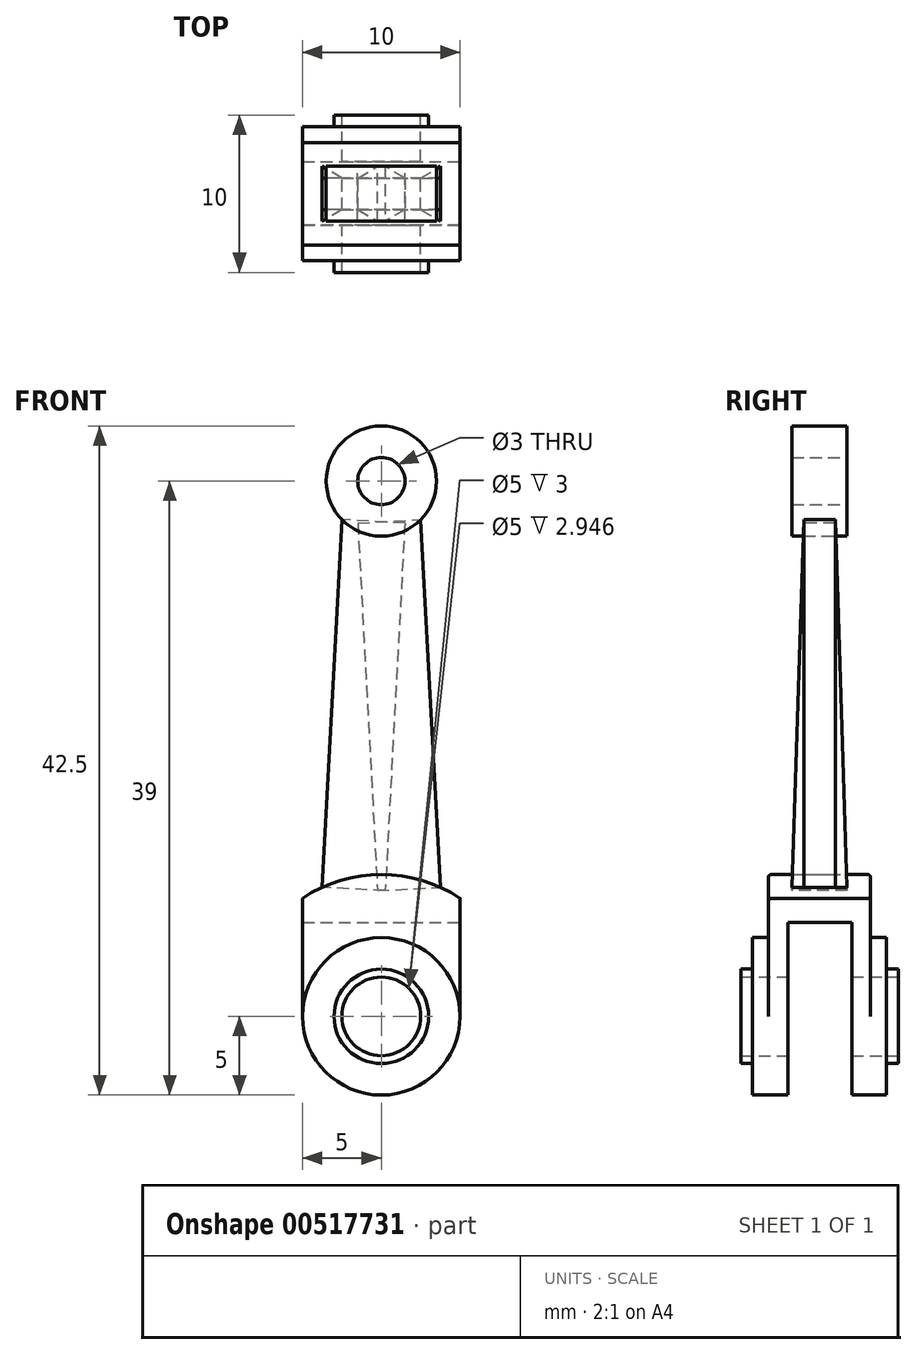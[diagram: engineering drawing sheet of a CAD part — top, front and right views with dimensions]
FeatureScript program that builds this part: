
annotation { "Feature Type Name" : "Feature", "Feature Type Description" : "" }
export const myFeature = defineFeature(function(context is Context, id is Id, definition is map)
    precondition{}
    {
        {
            var Q0;
            Q0=qCreatedBy(makeId("Front.planeOp"),FACE);
            var sketch = newSketch(context, id + "F0", { "sketchPlane" : qUnion([Q0])});
            skPoint(sketch, "E0", {"position": v(0, 0) * mm});
            skPoint(sketch, "E1", {"position": v(0, 34) * mm});
            skCircle(sketch, "E2", {"center": v(0, 34) * mm, "radius": 3.5 * mm});
            skCircle(sketch, "E3", {"center": v(0, 34) * mm, "radius": 1.5 * mm});
            skCircle(sketch, "E4", {"center": v(0, 0) * mm, "radius": 5 * mm});
            skCircle(sketch, "E5", {"center": v(0, 0) * mm, "radius": 3 * mm});
            skCircle(sketch, "E6", {"center": v(0, 0) * mm, "radius": 2.5 * mm});
            skLineSegment(sketch, "E7", {"start": v(-5, 7.5) * mm, "end": v(-5, 0) * mm});
            skLineSegment(sketch, "E8", {"start": v(5, 7.5) * mm, "end": v(5, 0) * mm});
            skArc(sketch, "E9", {"start": v(-5, 7.5) * mm, "mid": v(0, 9.01) * mm, "end": v(5, 7.5) * mm});
            skLineSegment(sketch, "E10", {"start": v(-3.75, 8.2) * mm, "end": v(3.75, 8.2) * mm, "construction": true});
            skPoint(sketch, "E11", {"position": v(0, 8.2) * mm});
            skLineSegment(sketch, "E12", {"start": v(0, 34) * mm, "end": v(0, 0) * mm, "construction": true});
            skLineSegment(sketch, "E13", {"start": v(-2.5, 31.55) * mm, "end": v(2.5, 31.55) * mm, "construction": true});
            skPoint(sketch, "E14", {"position": v(0, 31.55) * mm});
            skLineSegment(sketch, "E15", {"start": v(-2.5, 31.55) * mm, "end": v(-3.75, 8.2) * mm});
            skLineSegment(sketch, "E16", {"start": v(2.5, 31.55) * mm, "end": v(3.75, 8.2) * mm});
            skSolve(sketch);
        }
        {
            var Q0;
            {var subQ0=sQuery(id+"F0.wireOp",EDGE,"E7");Q0=makeQuery(id+"F0.imprint","IMPRINT",FACE,{"disambiguationData":[TD([[makeQuery(id+"F0.imprint","IMPRINT",EDGE,{"derivedFrom":subQ0}),1.0]])]});}
            extrude(context, id + "F1", {"entities" : qUnion([Q0]), "depth" : 6.5 * mm, "offsetDistance" : 25 * mm, "symmetric" : true});
        }
        {
            var Q0;
            Q0=makeQuery(id+"F0.imprint","IMPRINT",FACE,{"disambiguationData":[TD([[makeQuery(id+"F0.imprint","IMPRINT",EDGE,{"derivedFrom":sQuery(id+"F0.wireOp",EDGE,"E5")}),-1.0]])]});
            extrude(context, id + "F2", {"entities" : qUnion([Q0]), "operationType" : NewBodyOperationType.ADD, "depth" : 8.5 * mm, "offsetDistance" : 25 * mm, "symmetric" : true});
        }
        {
            var Q0;
            Q0=makeQuery(id+"F0.imprint","IMPRINT",FACE,{"disambiguationData":[TD([[makeQuery(id+"F0.imprint","IMPRINT",EDGE,{"derivedFrom":sQuery(id+"F0.wireOp",EDGE,"E5")}),1.0]])]});
            extrude(context, id + "F3", {"entities" : qUnion([Q0]), "operationType" : NewBodyOperationType.ADD, "depth" : 10 * mm, "offsetDistance" : 25 * mm, "symmetric" : true});
        }
        {
            var Q0;
            Q0=makeQuery(id+"F1.opExtrude","SWEPT_FACE",FACE,{"disambiguationData":[OSD([sQuery(id+"F0.wireOp",EDGE,"E8")])]});
            cPlane(context, id + "F4", {"entities" : qUnion([Q0]), "cplaneType" : CPlaneType.OFFSET, "offset" : 0 * mm, "width" : 150 * mm, "height" : 150 * mm});
        }
        {
            var Q0;
            Q0=qCreatedBy(id+"F4.planeOp",FACE);
            var sketch = newSketch(context, id + "F5", { "sketchPlane" : qUnion([Q0])});
            skLineSegment(sketch, "E17", {"start": v(-9.63, 0) * mm, "end": v(9.54, 0) * mm, "construction": true});
            skLineSegment(sketch, "E18", {"start": v(0, 12.88) * mm, "end": v(0, -10.63) * mm, "construction": true});
            skPoint(sketch, "E19", {"position": v(0, 6) * mm});
            skLineSegment(sketch, "E20", {"start": v(-2, 6) * mm, "end": v(2, 6) * mm});
            skLineSegment(sketch, "E21", {"start": v(-2, 6) * mm, "end": v(-2, -6.94) * mm});
            skLineSegment(sketch, "E22", {"start": v(2.05, 6) * mm, "end": v(2, -6.93) * mm});
            skPoint(sketch, "E23", {"position": v(0, -6.93) * mm});
            skLineSegment(sketch, "E24", {"start": v(-1.95, -6.93) * mm, "end": v(2, -6.93) * mm});
            skSolve(sketch);
        }
        {
            var Q0;
            Q0=qCreatedBy(id+"F4.planeOp",FACE);
            var sketch = newSketch(context, id + "F6", { "sketchPlane" : qUnion([Q0])});
            skLineSegment(sketch, "E25", {"start": v(-2, 5.98) * mm, "end": v(2.05, 5.98) * mm});
            skLineSegment(sketch, "E26", {"start": v(2.05, 5.98) * mm, "end": v(2.05, -6.96) * mm});
            skLineSegment(sketch, "E27", {"start": v(2.05, -6.96) * mm, "end": v(-2, -6.96) * mm});
            skLineSegment(sketch, "E28", {"start": v(-2, -6.96) * mm, "end": v(-2, 5.98) * mm});
            skSolve(sketch);
        }
        {
            var Q0;
            Q0=makeQuery(id+"F6.imprint","IMPRINT",FACE,{"disambiguationData":[TD([[makeQuery(id+"F6.imprint","IMPRINT",EDGE,{"derivedFrom":sQuery(id+"F6.wireOp",EDGE,"E25")}),-1.0]])]});
            extrude(context, id + "F7", {"entities" : qUnion([Q0]), "operationType" : NewBodyOperationType.REMOVE, "oppositeDirection" : true, "depth" : 10 * mm, "offsetDistance" : 25 * mm});
        }
        {
            var Q0;
            Q0=makeQuery(id+"F0.imprint","IMPRINT",FACE,{"disambiguationData":[TD([[makeQuery(id+"F0.imprint","IMPRINT",EDGE,{"derivedFrom":sQuery(id+"F0.wireOp",EDGE,"E2")}),1.0]])]});
            extrude(context, id + "F8", {"entities" : qUnion([Q0]), "depth" : 3.5 * mm, "offsetDistance" : 25 * mm, "symmetric" : true});
        }
        {
            var Q0;
            {var subQ0=sQuery(id+"F0.wireOp",EDGE,"E15");Q0=makeQuery(id+"F0.imprint","IMPRINT",FACE,{"disambiguationData":[TD([[makeQuery(id+"F0.imprint","IMPRINT",EDGE,{"derivedFrom":subQ0}),1.0]])]});}
            extrude(context, id + "F9", {"entities" : qUnion([Q0]), "depth" : 2 * mm, "offsetDistance" : 25 * mm, "symmetric" : true});
        }
        {
            var Q0;
            Q0=makeQuery(id+"F9.opExtrude","SWEPT_FACE",FACE,{"disambiguationData":[OSD([sQuery(id+"F0.wireOp",EDGE,"E16")])]});
            cPlane(context, id + "F10", {"entities" : qUnion([Q0]), "cplaneType" : CPlaneType.OFFSET, "offset" : 0 * mm, "width" : 150 * mm, "height" : 150 * mm});
        }
        {
            var Q0;
            Q0=qCreatedBy(id+"F10.planeOp",FACE);
            var sketch = newSketch(context, id + "F11", { "sketchPlane" : qUnion([Q0])});
            skLineSegment(sketch, "E29", {"start": v(-1.75, 7.98) * mm, "end": v(1.75, 7.98) * mm});
            skPoint(sketch, "E30", {"position": v(0, 7.98) * mm});
            skLineSegment(sketch, "E31", {"start": v(-1, 31.37) * mm, "end": v(1, 31.37) * mm});
            skPoint(sketch, "E32", {"position": v(0, 31.37) * mm});
            skLineSegment(sketch, "E33", {"start": v(-1, 31.37) * mm, "end": v(-1.75, 7.98) * mm});
            skLineSegment(sketch, "E34", {"start": v(1, 31.37) * mm, "end": v(1.75, 7.98) * mm});
            skSolve(sketch);
        }
        {
            var Q0;
            Q0=makeQuery(id+"F11.imprint","IMPRINT",FACE,{"disambiguationData":[TD([[makeQuery(id+"F11.imprint","IMPRINT",EDGE,{"derivedFrom":sQuery(id+"F11.wireOp",EDGE,"E29")}),1.0]])]});
            extrude(context, id + "F12", {"entities" : qUnion([Q0]), "oppositeDirection" : true, "depth" : 4 * mm, "offsetDistance" : 25 * mm});
        }
        {
            var Q0;
            Q0=makeQuery(id+"F9.opExtrude","SWEPT_FACE",FACE,{"disambiguationData":[OSD([sQuery(id+"F0.wireOp",EDGE,"E15")])]});
            cPlane(context, id + "F13", {"entities" : qUnion([Q0]), "cplaneType" : CPlaneType.OFFSET, "offset" : 0 * mm, "width" : 150 * mm, "height" : 150 * mm});
        }
        {
            var Q0;
            Q0=qCreatedBy(id+"F13.planeOp",FACE);
            var sketch = newSketch(context, id + "F14", { "sketchPlane" : qUnion([Q0])});
            skLineSegment(sketch, "E35", {"start": v(-1.75, 7.98) * mm, "end": v(1.75, 7.98) * mm});
            skLineSegment(sketch, "E36", {"start": v(-1, 31.37) * mm, "end": v(1, 31.37) * mm});
            skPoint(sketch, "E37", {"position": v(0, 7.98) * mm});
            skPoint(sketch, "E38", {"position": v(0, 31.37) * mm});
            skLineSegment(sketch, "E39", {"start": v(-1, 31.37) * mm, "end": v(-1.75, 7.98) * mm});
            skLineSegment(sketch, "E40", {"start": v(1, 31.37) * mm, "end": v(1.75, 7.98) * mm});
            skSolve(sketch);
        }
        {
            var Q0;
            Q0=makeQuery(id+"F14.imprint","IMPRINT",FACE,{"disambiguationData":[TD([[makeQuery(id+"F14.imprint","IMPRINT",EDGE,{"derivedFrom":sQuery(id+"F14.wireOp",EDGE,"E35")}),1.0]])]});
            extrude(context, id + "F15", {"entities" : qUnion([Q0]), "oppositeDirection" : true, "depth" : 4 * mm, "offsetDistance" : 25 * mm});
        }
        {
            var Q0;
            Q0=makeQuery(id+"F1.opExtrude","CAP_EDGE",EDGE,{"disambiguationData":[OSD([sQuery(id+"F0.wireOp",EDGE,"E9")])],"isStart":false});
            var Q1;
            Q1=makeQuery(id+"F1.opExtrude","CAP_EDGE",EDGE,{"disambiguationData":[OSD([sQuery(id+"F0.wireOp",EDGE,"E9")])],"isStart":true});
            fillet(context, id + "F16", {"entities" : qUnion([Q0, Q1]), "radius" : 0.2 * mm, "tangentPropagation" : true, "allowEdgeOverflow" : false});
        }
    });
